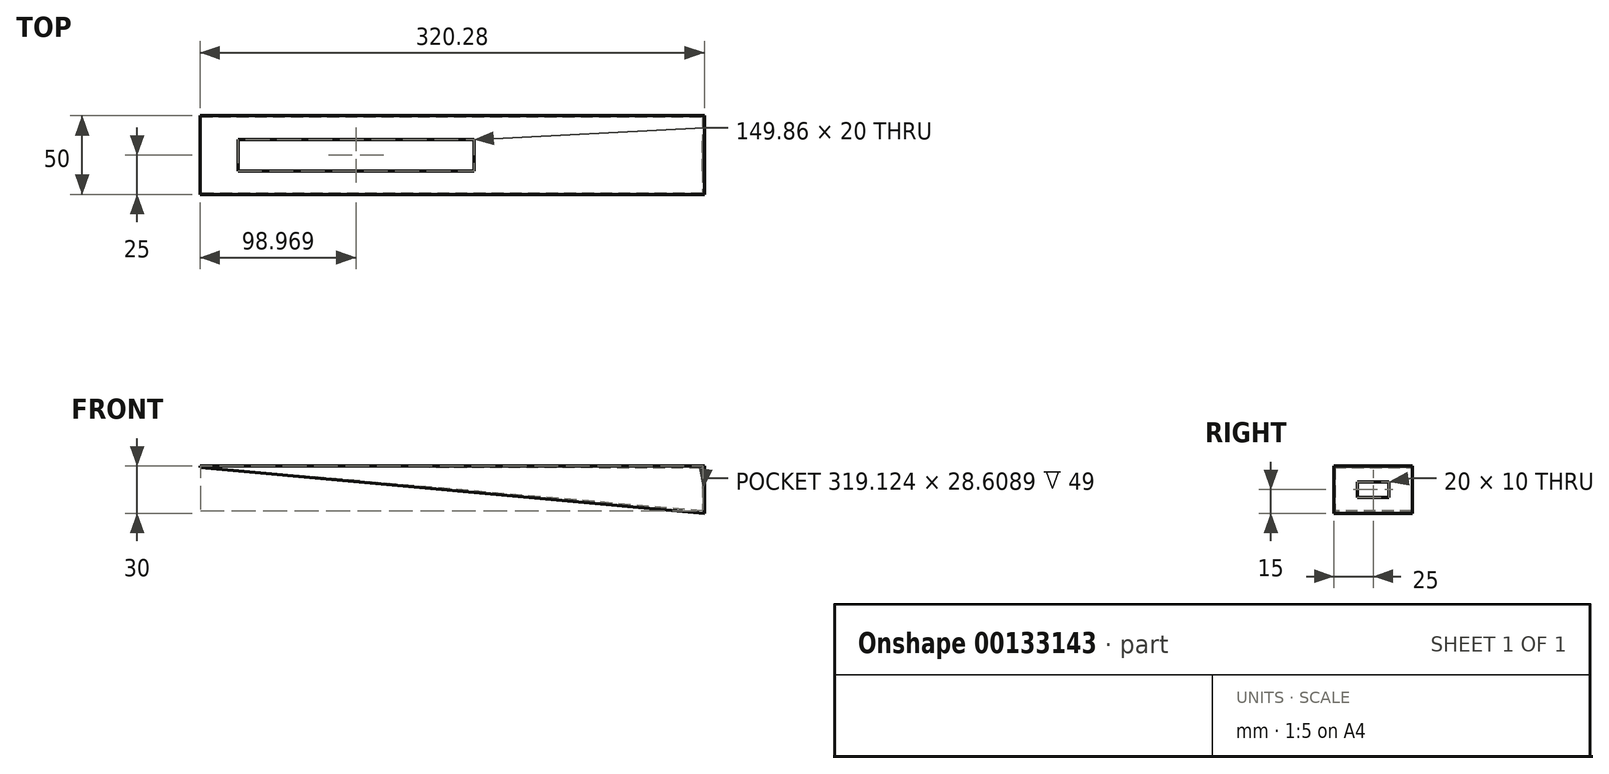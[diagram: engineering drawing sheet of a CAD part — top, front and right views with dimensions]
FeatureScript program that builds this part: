
annotation { "Feature Type Name" : "Feature", "Feature Type Description" : "" }
export const myFeature = defineFeature(function(context is Context, id is Id, definition is map)
    precondition{}
    {
        {
            var Q0;
            Q0=qCreatedBy(makeId("Front.planeOp"),FACE);
            var sketch = newSketch(context, id + "F0", { "sketchPlane" : qUnion([Q0])});
            skLineSegment(sketch, "E0", {"start": v(-69.66, 0) * mm, "end": v(250.34, 0) * mm});
            skLineSegment(sketch, "E1", {"start": v(-69.8, -0.9) * mm, "end": v(250.34, -30) * mm});
            skLineSegment(sketch, "E2", {"start": v(250.34, -30) * mm, "end": v(250.34, 0) * mm});
            skLineSegment(sketch, "E3", {"start": v(-69.66, -0.03) * mm, "end": v(249.33, -0.97) * mm});
            skLineSegment(sketch, "E4", {"start": v(249.33, -0.97) * mm, "end": v(249.25, -28.64) * mm});
            skLineSegment(sketch, "E5", {"start": v(249.25, -28.64) * mm, "end": v(-69.79, -0.83) * mm});
            skLineSegment(sketch, "E6", {"start": v(-69.66, -0.03) * mm, "end": v(-69.79, -0.83) * mm});
            skLineSegment(sketch, "E7", {"start": v(-69.94, -0.88) * mm, "end": v(-69.8, -0.9) * mm});
            skLineSegment(sketch, "E8", {"start": v(-69.8, 0) * mm, "end": v(-69.94, -0.88) * mm});
            skLineSegment(sketch, "E9", {"start": v(-69.8, 0) * mm, "end": v(-69.66, 0) * mm});
            skSolve(sketch);
        }
        {
            var Q0;
            Q0=makeQuery(id+"F0.imprint","IMPRINT",FACE,{"disambiguationData":[TD([[makeQuery(id+"F0.imprint","IMPRINT",EDGE,{"derivedFrom":sQuery(id+"F0.wireOp",EDGE,"hZ2UMt2E-fBOG-nuDn-IccN-yUAMeZouQCkQ")}),-1.0]])]});
            var Q1;
            Q1=makeQuery(id+"F0.imprint","IMPRINT",FACE,{"disambiguationData":[TD([[makeQuery(id+"F0.imprint","IMPRINT",EDGE,{"derivedFrom":sQuery(id+"F0.wireOp",EDGE,"E0")}),-1.0]])]});
            var Q2;
            Q2=makeQuery(id+"F0.imprint","IMPRINT",FACE,{"disambiguationData":[TD([[makeQuery(id+"F0.imprint","IMPRINT",EDGE,{"derivedFrom":sQuery(id+"F0.wireOp",EDGE,"E3")}),-1.0]])]});
            extrude(context, id + "F1", {"entities" : qUnion([Q0, Q1, Q2]), "endBound" : BoundingType.SYMMETRIC, "depth" : 50 * mm});
        }
        {
            var Q0;
            Q0=makeQuery(id+"F0.imprint","IMPRINT",FACE,{"disambiguationData":[TD([[makeQuery(id+"F0.imprint","IMPRINT",EDGE,{"derivedFrom":sQuery(id+"F0.wireOp",EDGE,"E3")}),-1.0]])]});
            extrude(context, id + "F2", {"entities" : qUnion([Q0]), "operationType" : NewBodyOperationType.REMOVE, "endBound" : BoundingType.SYMMETRIC, "oppositeDirection" : true, "depth" : 49 * mm});
        }
        {
            var Q0;
            Q0=makeQuery(id+"F1.opExtrude","SWEPT_FACE",FACE,{"disambiguationData":[OSD([sQuery(id+"F0.wireOp",EDGE,"E2")])]});
            var sketch = newSketch(context, id + "F3", { "sketchPlane" : qUnion([Q0])});
            skLineSegment(sketch, "E10.bottom", {"start": v(-10, -10) * mm, "end": v(10, -10) * mm});
            skLineSegment(sketch, "E10.top", {"start": v(-10, -20) * mm, "end": v(10, -20) * mm});
            skLineSegment(sketch, "E10.left", {"start": v(-10, -10) * mm, "end": v(-10, -20) * mm});
            skLineSegment(sketch, "E10.right", {"start": v(10, -10) * mm, "end": v(10, -20) * mm});
            skSolve(sketch);
        }
        {
            var Q0;
            Q0=makeQuery(id+"F3.imprint","IMPRINT",FACE,{"disambiguationData":[TD([[makeQuery(id+"F3.imprint","IMPRINT",EDGE,{"derivedFrom":sQuery(id+"F3.wireOp",EDGE,"E10.bottom")}),-1.0]])]});
            extrude(context, id + "F4", {"entities" : qUnion([Q0]), "operationType" : NewBodyOperationType.REMOVE, "endBound" : BoundingType.UP_TO_NEXT, "oppositeDirection" : true, "depth" : 25 * mm});
        }
        {
            var Q0;
            Q0=makeQuery(id+"F1.opExtrude","SWEPT_FACE",FACE,{"disambiguationData":[OSD([sQuery(id+"F0.wireOp",EDGE,"E0"),sQuery(id+"F0.wireOp",EDGE,"E9")])]});
            var sketch = newSketch(context, id + "F5", { "sketchPlane" : qUnion([Q0])});
            skLineSegment(sketch, "E11.bottom", {"start": v(-45.9, 10) * mm, "end": v(103.96, 10) * mm});
            skLineSegment(sketch, "E11.top", {"start": v(-45.9, -10) * mm, "end": v(103.96, -10) * mm});
            skLineSegment(sketch, "E11.left", {"start": v(-45.9, 10) * mm, "end": v(-45.9, -10) * mm});
            skLineSegment(sketch, "E11.right", {"start": v(103.96, 10) * mm, "end": v(103.96, -10) * mm});
            skSolve(sketch);
        }
        {
            var Q0;
            Q0=makeQuery(id+"F5.imprint","IMPRINT",FACE,{"disambiguationData":[TD([[makeQuery(id+"F5.imprint","IMPRINT",EDGE,{"derivedFrom":sQuery(id+"F5.wireOp",EDGE,"E11.bottom")}),-1.0]])]});
            extrude(context, id + "F6", {"entities" : qUnion([Q0]), "operationType" : NewBodyOperationType.REMOVE, "endBound" : BoundingType.UP_TO_NEXT, "oppositeDirection" : true, "depth" : 25 * mm});
        }
    });
